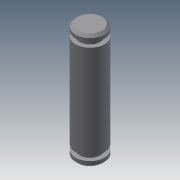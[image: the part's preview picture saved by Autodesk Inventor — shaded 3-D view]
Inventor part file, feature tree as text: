
AUTODESK INVENTOR PART (.ipt)
format: ipt  version: 2013 (Build 170138000, 138)  size: 94,208 bytes
history: native  units: mm
features: revolve x1, chamfer x1, sketch x1
ambient origin geometry x8: Origin, YZ Plane, XZ Plane, XY Plane, X Axis, Y Axis, Z Axis, Center Point
bodies: Solid1 (feature_tree)
feature tree (3):
  revolve  "Revolution1"  [1 undecoded]
  chamfer  "Chamfer1"  Distance=0.85mm
  sketch  "Sketch1"  dims[d12=19.5mm d13=1.0mm d14=0.85mm d16=1.0mm d17=90.0deg d18=0.5mm d19=2.0mm d20=45.0deg]
note: 1 required parameter value undecoded (feature->parameter linkage not recoverable at this tier; creation-order binding heuristic only, values carry confidence <= 0.55)
